# Revit family: RUFO-390-1800-840-Zx
name_source: partatom
category: Oprawy oświetleniowe
revit_build: Autodesk Revit 2017 (Build: 20190507_1515(x64)
units: mm (PartAtom-declared; Revit-internal decimal feet)

## family parameters
Numer OmniClass = 23.80.70.11
Obiekt nadrzędny = Powierzchnia
Punkt obliczania pomieszczeń = Nie
Tnij formami wycięć po wczytaniu = Tak
Typ części = Normalny
Tytuł OmniClass = Luminaries for Internal Lighting
Współdzielony = Nie
Wymiar okrągłego złącza = Użyj średnicy
Źródło światła = Tak

## types (9) — shared parameters
Emituj kształt widoczny w renderingu = Nie
Emituj ze średnicy okręgu = 370 mm  [stored 1.21391 ft]
Filtr koloru = 16777215
Kod zespołu = D5020200
Lampa = LED
Obciążenie pozorne = 14 VA
Odchylenie kierunku = 90.00°
Plik sieci fotometrycznej = RUFO 3901800-840-Z.IES
Producent = RIDI Leuchten GmbH
URL = www.ridi.de
Zmiana temperatury barwowej przyciemniania lampy = <Brak>
brand = RIDI
conformity mark = CE
electrical safety class = 1
height = 85 mm  [stored 0.278871 ft]
ingress protection (IP) code = IP20
length = 370 mm  [stored 1.21391 ft]
nominal frequency = 50-60Hz
nominal voltage = 230
rated input power = 14
voltage type (AC, DC, UC) = AC
width = 370 mm  [stored 1.21391 ft]
zero-valued in all types: Domyślna rzędna

## per-type parameters (varying)
| type | Model | weight |
| RUFO 390/1800-840 Z | 0420764 | 1.2kg |
| RUFO 390/1800-840 Z-DALI | 0430764 | 1.2kg |
| RUFO 390/1800-840 Z-2K | 0420765 | 1.2kg |
| RUFO 390/1800-840 Z-2K-EDS3 | 0420765//377 | 1.2kg |
| RUFO 390/1800-840 Z-2K-RS | 0420765//396 | 1.2kg |
| RUFO 390/1800-840 Z-2K-RS-EDS3 | 0420765//377396 | 1.2kg |
| RUFO 390/1800-840 Z-EDS3 | 0420764//377 | 1.37kg |
| RUFO 390/1800-840 Z-RS | 0420764//396 | 1.2kg |
| RUFO 390/1800-840 Z-RS-EDS3 | 0420764//377396 | 1.2kg |

note: column(s) folded — value = type name in every type: product name

note: [stored X ft] marks values corroborated as IEEE doubles in the binary element streams (Revit-internal decimal feet)
